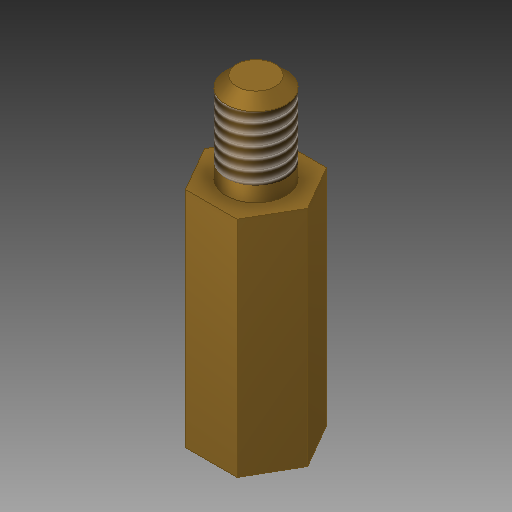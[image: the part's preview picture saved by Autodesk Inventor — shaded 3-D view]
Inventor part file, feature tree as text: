
AUTODESK INVENTOR PART (.ipt)
format: ipt  version: 2018 (Build 220112000, 112)  size: 130,560 bytes
history: native  units: mm
features: sketch x2, extrude x2, hole x1, thread x1, chamfer x1
ambient origin geometry x8: Origin, YZ Plane, XZ Plane, XY Plane, X Axis, Y Axis, Z Axis, Center Point
bodies: Solid1 (feature_tree)
feature tree (7):
  sketch  "Sketch1"  dims[d0=3.0mm d1=15.0mm d2=0.0mm]
  extrude  "Extrusion1"  Depth=15.0mm TaperAngle=0.0deg
  hole  "Hole2"  [1 undecoded]
  extrude  "Extrusion2"  Depth=6.0mm TaperAngle=0.0deg
  thread  "Thread1"  [1 undecoded]
  chamfer  "Chamfer1"  Distance=2.0mm Angle=45.0deg
  sketch  "Sketch3"  dims[d10=3.242mm d11=8.0mm d12=4.0mm d13=2.0mm d14=90.0deg d15=11.8mm d16=20.594885mm d17=4.0mm d18=6.0mm d19=0.0mm d20=5.0mm d21=0.0mm d22=0.7mm d23=2.0mm d24=45.0deg]
note: 2 required parameter values undecoded (feature->parameter linkage not recoverable at this tier; creation-order binding heuristic only, values carry confidence <= 0.55)
